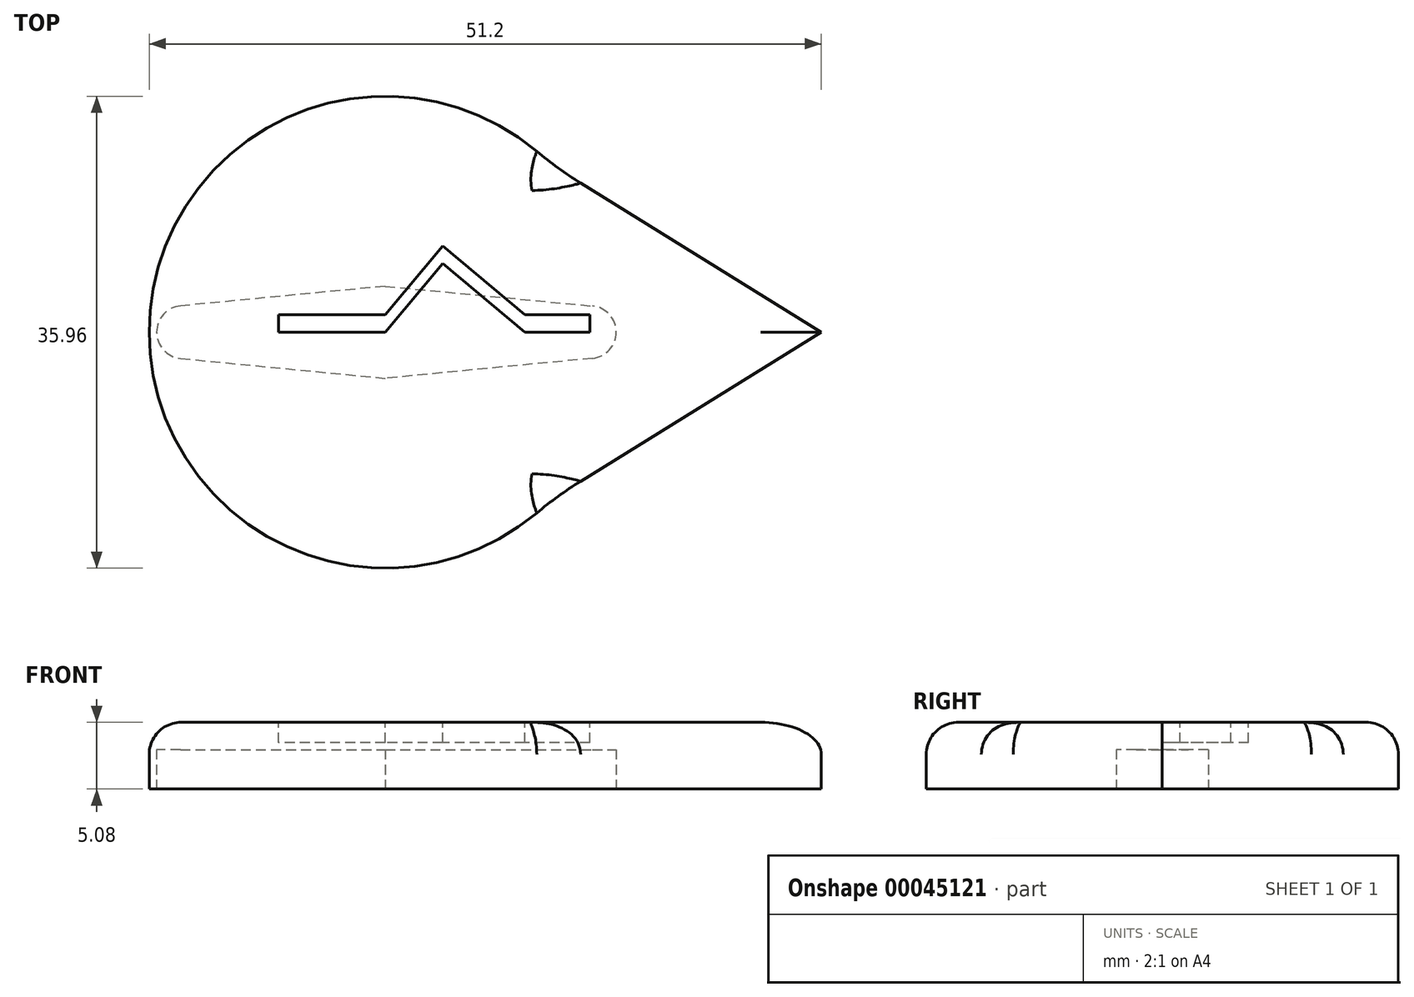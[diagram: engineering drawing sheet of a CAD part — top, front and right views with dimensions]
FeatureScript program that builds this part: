
annotation { "Feature Type Name" : "Feature", "Feature Type Description" : "" }
export const myFeature = defineFeature(function(context is Context, id is Id, definition is map)
    precondition{}
    {
        {
            var Q0;
            Q0=qCreatedBy(makeId("Top.planeOp"),FACE);
            var sketch = newSketch(context, id + "F0", { "sketchPlane" : qUnion([Q0])});
            skCircle(sketch, "E0", {"center": v(0, 0) * mm, "radius": 17.98 * mm});
            skLineSegment(sketch, "E1", {"start": v(-17.98, 0) * mm, "end": v(17.98, 0) * mm});
            skLineSegment(sketch, "E2", {"start": v(0, 0) * mm, "end": v(12.71, 12.71) * mm});
            skLineSegment(sketch, "E3", {"start": v(0, 0) * mm, "end": v(12.71, -12.71) * mm});
            skLineSegment(sketch, "E4", {"start": v(17.98, 0) * mm, "end": v(33.22, 0) * mm});
            skLineSegment(sketch, "E5", {"start": v(12.71, 12.71) * mm, "end": v(33.22, 0) * mm});
            skLineSegment(sketch, "E6", {"start": v(12.71, -12.71) * mm, "end": v(33.22, 0) * mm});
            skSolve(sketch);
        }
        {
            var Q0;
            Q0=qSketchRegion(id+"F0",true);
            extrude(context, id + "F1", {"entities" : qUnion([Q0]), "depth" : 5.08 * mm});
        }
        {
            var Q0;
            Q0=makeQuery(id+"F1.opExtrude","CAP_EDGE",EDGE,{"disambiguationData":[OSD([sQuery(id+"F0.wireOp",EDGE,"E0")])],"isStart":false});
            var Q1;
            Q1=makeQuery(id+"F1.opExtrude","CAP_EDGE",EDGE,{"disambiguationData":[OSD([sQuery(id+"F0.wireOp",EDGE,"E6")])],"isStart":false});
            var Q2;
            Q2=makeQuery(id+"F1.opExtrude","CAP_EDGE",EDGE,{"disambiguationData":[OSD([sQuery(id+"F0.wireOp",EDGE,"E5")])],"isStart":false});
            fillet(context, id + "F2", {"entities" : qUnion([Q0, Q1, Q2]), "radius" : 2.43 * mm, "tangentPropagation" : true, "allowEdgeOverflow" : false});
        }
        {
            var Q0;
            Q0=makeQuery(id+"F1.opExtrude","SWEPT_EDGE",EDGE,{"disambiguationData":[OSD([sQuery(id+"F0.wireOp",EDGE,"E0"),sQuery(id+"F0.wireOp",EDGE,"E3"),sQuery(id+"F0.wireOp",EDGE,"E6")])]});
            var Q1;
            Q1=makeQuery(id+"F2.opFillet","BLEND_EDGE",EDGE,{"blendedFrom":[makeQuery(id+"F1.opExtrude","CAP_EDGE",EDGE,{"disambiguationData":[OSD([sQuery(id+"F0.wireOp",EDGE,"E0")])],"isStart":false}),makeQuery(id+"F1.opExtrude","CAP_EDGE",EDGE,{"disambiguationData":[OSD([sQuery(id+"F0.wireOp",EDGE,"E6")])],"isStart":false})],"blendedInto":[]});
            var Q2;
            Q2=makeQuery(id+"F1.opExtrude","SWEPT_EDGE",EDGE,{"disambiguationData":[OSD([sQuery(id+"F0.wireOp",EDGE,"E0"),sQuery(id+"F0.wireOp",EDGE,"E2"),sQuery(id+"F0.wireOp",EDGE,"E5")])]});
            var Q3;
            Q3=makeQuery(id+"F2.opFillet","BLEND_EDGE",EDGE,{"blendedFrom":[makeQuery(id+"F1.opExtrude","CAP_EDGE",EDGE,{"disambiguationData":[OSD([sQuery(id+"F0.wireOp",EDGE,"E0")])],"isStart":false}),makeQuery(id+"F1.opExtrude","CAP_EDGE",EDGE,{"disambiguationData":[OSD([sQuery(id+"F0.wireOp",EDGE,"E5")])],"isStart":false})],"blendedInto":[]});
            fillet(context, id + "F3", {"entities" : qUnion([Q0, Q1, Q2, Q3]), "radius" : 29.01 * mm, "tangentPropagation" : true, "allowEdgeOverflow" : false});
        }
        {
            var Q0;
            Q0=makeQuery(id+"F1.opExtrude","CAP_FACE",FACE,{"disambiguationData":[OSD([sQuery(id+"F0.wireOp",EDGE,"E0"),sQuery(id+"F0.wireOp",EDGE,"E5"),sQuery(id+"F0.wireOp",EDGE,"E6")])],"isStart":false});
            var sketch = newSketch(context, id + "F4", { "sketchPlane" : qUnion([Q0])});
            skLineSegment(sketch, "E7", {"start": v(0, 0) * mm, "end": v(-8.12, 0) * mm});
            skLineSegment(sketch, "E8", {"start": v(-8.12, 0) * mm, "end": v(-8.12, 1.33) * mm});
            skLineSegment(sketch, "E9", {"start": v(-8.12, 1.33) * mm, "end": v(0, 1.33) * mm});
            skLineSegment(sketch, "E10", {"start": v(0, 1.33) * mm, "end": v(4.37, 6.57) * mm});
            skLineSegment(sketch, "E11", {"start": v(4.37, 6.57) * mm, "end": v(10.64, 1.33) * mm});
            skLineSegment(sketch, "E12", {"start": v(10.64, 1.33) * mm, "end": v(15.57, 1.33) * mm});
            skLineSegment(sketch, "E13", {"start": v(15.57, 1.33) * mm, "end": v(15.57, 0) * mm});
            skLineSegment(sketch, "E14", {"start": v(15.57, 0) * mm, "end": v(10.64, 0) * mm});
            skLineSegment(sketch, "E15", {"start": v(10.64, 0) * mm, "end": v(4.37, 5.23) * mm});
            skLineSegment(sketch, "E16", {"start": v(4.37, 5.23) * mm, "end": v(0, 0) * mm});
            skSolve(sketch);
        }
        {
            var Q0;
            Q0=makeQuery(id+"F4.imprint","IMPRINT",FACE,{"disambiguationData":[TD([[makeQuery(id+"F4.imprint","IMPRINT",EDGE,{"derivedFrom":sQuery(id+"F4.wireOp",EDGE,"E7")}),-1.0]])]});
            extrude(context, id + "F5", {"entities" : qUnion([Q0]), "operationType" : NewBodyOperationType.REMOVE, "oppositeDirection" : true, "depth" : 1.55 * mm});
        }
        {
            var Q0;
            Q0=makeQuery(id+"F1.opExtrude","CAP_FACE",FACE,{"disambiguationData":[OSD([sQuery(id+"F0.wireOp",EDGE,"E0"),sQuery(id+"F0.wireOp",EDGE,"E5"),sQuery(id+"F0.wireOp",EDGE,"E6")])],"isStart":true});
            var sketch = newSketch(context, id + "F6", { "sketchPlane" : qUnion([Q0])});
            skLineSegment(sketch, "E17", {"start": v(-15.6, 2) * mm, "end": v(0, 3.52) * mm});
            skLineSegment(sketch, "E18", {"start": v(0, -3.5) * mm, "end": v(-15.6, -2) * mm});
            skLineSegment(sketch, "E19", {"start": v(0, -3.5) * mm, "end": v(15.8, -2) * mm});
            skLineSegment(sketch, "E20", {"start": v(15.8, 2) * mm, "end": v(0, 3.52) * mm});
            skArc(sketch, "E21", {"start": v(15.8, -2) * mm, "mid": v(17.6, 0) * mm, "end": v(15.8, 2) * mm});
            skArc(sketch, "E22", {"start": v(-15.6, 2) * mm, "mid": v(-17.42, 0) * mm, "end": v(-15.6, -2) * mm});
            skSolve(sketch);
        }
        {
            var Q0;
            Q0=makeQuery(id+"F6.imprint","IMPRINT",FACE,{"disambiguationData":[TD([[makeQuery(id+"F6.imprint","IMPRINT",EDGE,{"derivedFrom":sQuery(id+"F6.wireOp",EDGE,"E17")}),-1.0]])]});
            extrude(context, id + "F7", {"entities" : qUnion([Q0]), "operationType" : NewBodyOperationType.REMOVE, "oppositeDirection" : true, "depth" : 3 * mm});
        }
    });
